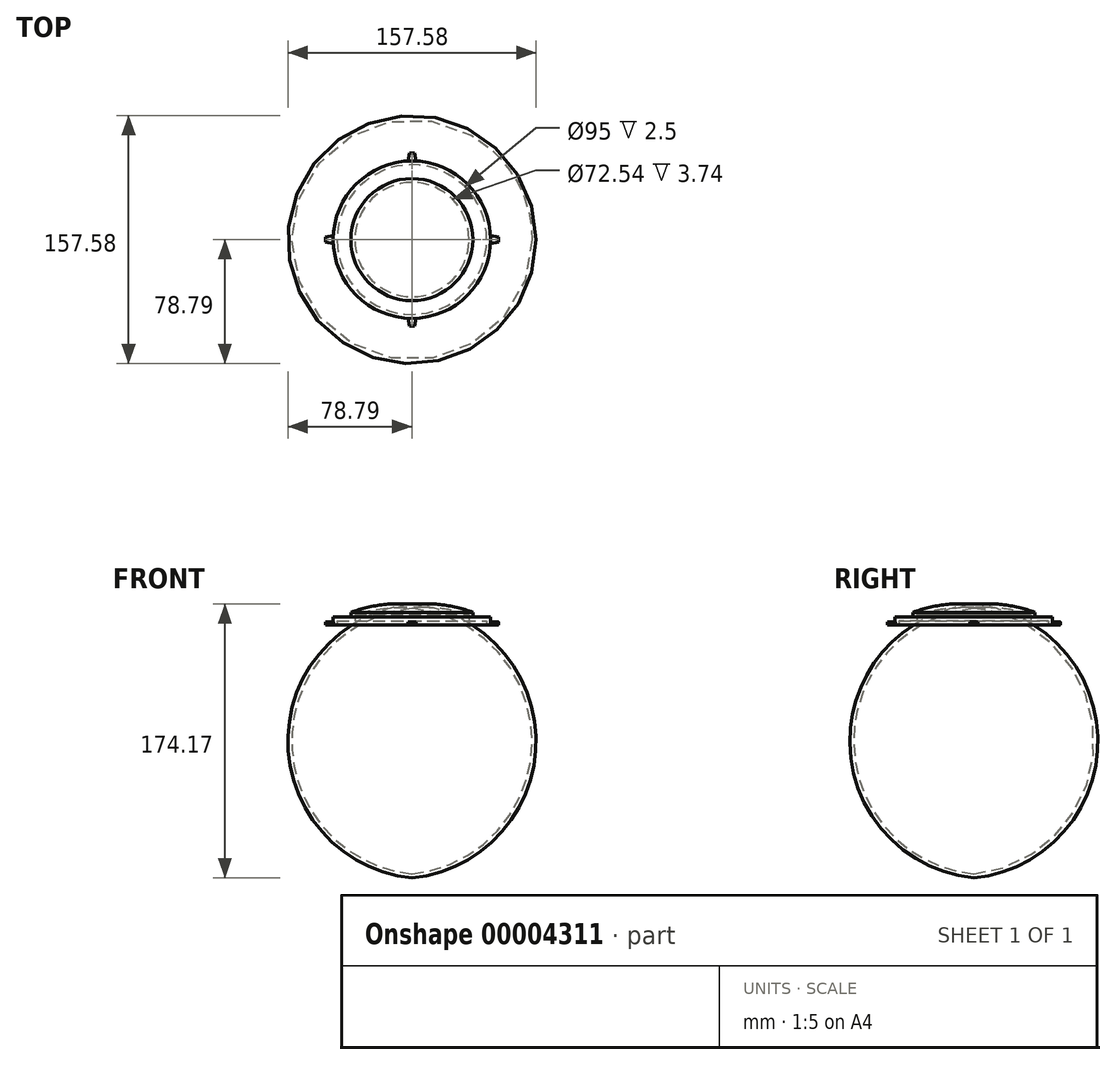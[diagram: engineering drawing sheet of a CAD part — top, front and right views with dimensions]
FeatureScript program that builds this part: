
annotation { "Feature Type Name" : "Feature", "Feature Type Description" : "" }
export const myFeature = defineFeature(function(context is Context, id is Id, definition is map)
    precondition{}
    {
        {
            var Q0;
            Q0=qCreatedBy(makeId("Front.planeOp"),FACE);
            var sketch = newSketch(context, id + "F0", { "sketchPlane" : qUnion([Q0])});
            skLineSegment(sketch, "E0", {"start": v(0, 0) * mm, "end": v(-50, 0) * mm});
            skLineSegment(sketch, "E1", {"start": v(-50, 0) * mm, "end": v(-55, 0) * mm});
            skArc(sketch, "E2", {"start": v(0, 13) * mm, "mid": v(-19.67, 12.7) * mm, "end": v(-38.77, 8) * mm});
            skLineSegment(sketch, "E3", {"start": v(0, 0) * mm, "end": v(0, 13) * mm});
            skLineSegment(sketch, "E4.0", {"start": v(-50, 2) * mm, "end": v(-55, 2) * mm});
            skLineSegment(sketch, "E5", {"start": v(-55, 2) * mm, "end": v(-55, 0) * mm});
            skLineSegment(sketch, "E6", {"start": v(-50, 2) * mm, "end": v(-50, 2.92) * mm});
            skLineSegment(sketch, "E7.0", {"start": v(0, 5) * mm, "end": v(-50, 5) * mm});
            skLineSegment(sketch, "E8.0", {"start": v(4.8, 8) * mm, "end": v(-50, 8) * mm});
            skLineSegment(sketch, "E9", {"start": v(-38.77, 8) * mm, "end": v(-38.77, 5) * mm});
            skArc(sketch, "E10.trimOffspring", {"start": v(-45.9, 5) * mm, "mid": v(-47.96, 3.99) * mm, "end": v(-50, 2.92) * mm, "construction": true});
            skLineSegment(sketch, "E11", {"start": v(0, 0) * mm, "end": v(55, 0) * mm});
            skLineSegment(sketch, "E12.0", {"start": v(0, 2) * mm, "end": v(55, 2) * mm});
            skLineSegment(sketch, "E13.0", {"start": v(0, 5) * mm, "end": v(55, 5) * mm});
            skLineSegment(sketch, "E14", {"start": v(-50, 5) * mm, "end": v(-50, 2.92) * mm});
            skSolve(sketch);
        }
        {
            var Q0;
            Q0=qCreatedBy(makeId("Top.planeOp"),FACE);
            var sketch = newSketch(context, id + "F1", { "sketchPlane" : qUnion([Q0])});
            skLineSegment(sketch, "E15.0", {"start": v(-50, 50) * mm, "end": v(-50, -50) * mm, "construction": true});
            skLineSegment(sketch, "E16.0", {"start": v(50, 50) * mm, "end": v(50, -50) * mm, "construction": true});
            skLineSegment(sketch, "E17.0", {"start": v(-50, -50) * mm, "end": v(50, -50) * mm, "construction": true});
            skLineSegment(sketch, "E18.0", {"start": v(-50, 50) * mm, "end": v(50, 50) * mm, "construction": true});
            skLineSegment(sketch, "E19.0", {"start": v(-5, 55) * mm, "end": v(-5, 49.75) * mm, "construction": true});
            skLineSegment(sketch, "E20.0", {"start": v(5, 55) * mm, "end": v(5, 49.75) * mm, "construction": true});
            skLineSegment(sketch, "E21.trimOffspring", {"start": v(-5, -49.75) * mm, "end": v(-5, -55) * mm, "construction": true});
            skLineSegment(sketch, "E22.trimOffspring", {"start": v(5, -49.75) * mm, "end": v(5, -55) * mm, "construction": true});
            skLineSegment(sketch, "E23.trimOffspring", {"start": v(49.75, 5) * mm, "end": v(55, 5) * mm, "construction": true});
            skLineSegment(sketch, "E24.0", {"start": v(-55, 55) * mm, "end": v(-55, -55) * mm, "construction": true});
            skLineSegment(sketch, "E25.0", {"start": v(-55, -55) * mm, "end": v(55, -55) * mm, "construction": true});
            skLineSegment(sketch, "E26.0", {"start": v(55, 55) * mm, "end": v(55, -55) * mm, "construction": true});
            skLineSegment(sketch, "E27.0", {"start": v(-55, 55) * mm, "end": v(55, 55) * mm, "construction": true});
            skLineSegment(sketch, "E28.0", {"start": v(-55, 0) * mm, "end": v(-50, 0) * mm, "construction": true});
            skCircle(sketch, "E29", {"center": v(0, 0) * mm, "radius": 55 * mm});
            skCircle(sketch, "E30", {"center": v(0, 0) * mm, "radius": 50 * mm});
            skLineSegment(sketch, "E31.0", {"start": v(0, -50) * mm, "end": v(0, -55) * mm, "construction": true});
            skLineSegment(sketch, "E32.0", {"start": v(50, 0) * mm, "end": v(55, 0) * mm, "construction": true});
            skLineSegment(sketch, "E33.0", {"start": v(0, 55) * mm, "end": v(0, 50) * mm, "construction": true});
            skLineSegment(sketch, "E34.0", {"start": v(50, -1.5) * mm, "end": v(55, -1.5) * mm, "construction": true});
            skLineSegment(sketch, "E35.0", {"start": v(50, 1.5) * mm, "end": v(55, 1.5) * mm, "construction": true});
            skLineSegment(sketch, "E36.0", {"start": v(49.04, 2.5) * mm, "end": v(55, 2.5) * mm, "construction": true});
            skLineSegment(sketch, "E37.0", {"start": v(49.48, -2.5) * mm, "end": v(55, -2.5) * mm, "construction": true});
            skLineSegment(sketch, "E38", {"start": v(-49.26, 2.64) * mm, "end": v(-55, 1.49) * mm});
            skLineSegment(sketch, "E39", {"start": v(-49.38, -2.6) * mm, "end": v(-55, -1.49) * mm});
            skLineSegment(sketch, "E40", {"start": v(48.47, -2.78) * mm, "end": v(55, -1.49) * mm});
            skLineSegment(sketch, "E41", {"start": v(48.17, 2.84) * mm, "end": v(55, 1.49) * mm});
            skLineSegment(sketch, "E42.0", {"start": v(-1.5, -48.6) * mm, "end": v(-1.5, -55) * mm, "construction": true});
            skLineSegment(sketch, "E43.0", {"start": v(1.5, -48.4) * mm, "end": v(1.5, -55) * mm, "construction": true});
            skLineSegment(sketch, "E44.0", {"start": v(-2.5, -48.6) * mm, "end": v(-2.5, -55) * mm, "construction": true});
            skLineSegment(sketch, "E45.0", {"start": v(2.5, -48.4) * mm, "end": v(2.5, -55) * mm, "construction": true});
            skLineSegment(sketch, "E46", {"start": v(-2.73, -48.72) * mm, "end": v(-1.49, -55) * mm});
            skLineSegment(sketch, "E47", {"start": v(2.75, -48.63) * mm, "end": v(1.49, -55) * mm});
            skLineSegment(sketch, "E48.0", {"start": v(-1.5, 55) * mm, "end": v(-1.5, 49.02) * mm, "construction": true});
            skLineSegment(sketch, "E49.0", {"start": v(1.5, 55) * mm, "end": v(1.5, 49.18) * mm, "construction": true});
            skLineSegment(sketch, "E50.0", {"start": v(-2.5, 55) * mm, "end": v(-2.5, 49.16) * mm, "construction": true});
            skLineSegment(sketch, "E51.0", {"start": v(2.5, 55) * mm, "end": v(2.5, 49.11) * mm, "construction": true});
            skLineSegment(sketch, "E52", {"start": v(-2.75, 48.62) * mm, "end": v(-1.49, 55) * mm});
            skLineSegment(sketch, "E53", {"start": v(2.77, 48.54) * mm, "end": v(1.49, 55) * mm});
            skCircle(sketch, "E54.0", {"center": v(0, 0) * mm, "radius": 54.9 * mm});
            skSolve(sketch);
        }
        {
            var Q0;
            {var subQ6=sQuery(id+"F0.wireOp",EDGE,"E0");Q0=makeQuery(id+"F0.imprint","IMPRINT",FACE,{"disambiguationData":[TD([[makeQuery(id+"F0.imprint","IMPRINT",EDGE,{"derivedFrom":subQ6}),-1.0]])]});}
            var Q1;
            {var subQ0=sQuery(id+"F0.wireOp",EDGE,"E9");Q1=makeQuery(id+"F0.imprint","IMPRINT",FACE,{"disambiguationData":[TD([[makeQuery(id+"F0.imprint","IMPRINT",EDGE,{"derivedFrom":subQ0}),1.0]])]});}
            var Q2;
            {var subQ3=sQuery(id+"F0.wireOp",EDGE,"E2");Q2=makeQuery(id+"F0.imprint","IMPRINT",FACE,{"disambiguationData":[TD([[makeQuery(id+"F0.imprint","IMPRINT",EDGE,{"derivedFrom":subQ3}),1.0]])]});}
            var Q3;
            Q3=sQuery(id+"F0.wireOp",EDGE,"E3");
            revolve(context, id + "F2", {"entities" : qUnion([Q0, Q1, Q2]), "axis" : qUnion([Q3]), "revolveType" : RevolveType.FULL});
        }
        {
            var Q0;
            {var subQ3=sQuery(id+"F1.wireOp",EDGE,"E39");var subQ5=sQuery(id+"F1.wireOp",EDGE,"E30");var subQ7=makeQuery(id+"F1.imprint","INTERSECT",VERTEX,{"derivedFrom":[subQ5,subQ3]});Q0=makeQuery(id+"F1.imprint","IMPRINT",FACE,{"disambiguationData":[TD([[makeQuery(id+"F1.imprint","IMPRINT",EDGE,{"disambiguationData":[TD([[subQ7,-1.0]])],"derivedFrom":subQ5}),-1.0]])]});}
            var Q1;
            {var subQ1=sQuery(id+"F1.wireOp",EDGE,"E52");var subQ5=sQuery(id+"F1.wireOp",EDGE,"E30");var subQ6=makeQuery(id+"F1.imprint","INTERSECT",VERTEX,{"derivedFrom":[subQ5,subQ1]});Q1=makeQuery(id+"F1.imprint","IMPRINT",FACE,{"disambiguationData":[TD([[makeQuery(id+"F1.imprint","IMPRINT",EDGE,{"disambiguationData":[TD([[subQ6,-1.0]])],"derivedFrom":subQ5}),-1.0]])]});}
            var Q2;
            {var subQ1=sQuery(id+"F1.wireOp",EDGE,"E53");var subQ5=sQuery(id+"F1.wireOp",EDGE,"E30");var subQ6=makeQuery(id+"F1.imprint","INTERSECT",VERTEX,{"derivedFrom":[subQ5,subQ1]});Q2=makeQuery(id+"F1.imprint","IMPRINT",FACE,{"disambiguationData":[TD([[makeQuery(id+"F1.imprint","IMPRINT",EDGE,{"disambiguationData":[TD([[subQ6,1.0]])],"derivedFrom":subQ5}),-1.0]])]});}
            var Q3;
            {var subQ1=sQuery(id+"F1.wireOp",EDGE,"E47");var subQ5=sQuery(id+"F1.wireOp",EDGE,"E30");var subQ6=makeQuery(id+"F1.imprint","INTERSECT",VERTEX,{"derivedFrom":[subQ5,subQ1]});Q3=makeQuery(id+"F1.imprint","IMPRINT",FACE,{"disambiguationData":[TD([[makeQuery(id+"F1.imprint","IMPRINT",EDGE,{"disambiguationData":[TD([[subQ6,-1.0]])],"derivedFrom":subQ5}),-1.0]])]});}
            var Q4;
            {var subQ3=sQuery(id+"F1.wireOp",EDGE,"E39");var subQ5=sQuery(id+"F1.wireOp",EDGE,"E29");var subQ7=makeQuery(id+"F1.imprint","INTERSECT",VERTEX,{"derivedFrom":[subQ3,subQ5]});Q4=makeQuery(id+"F1.imprint","IMPRINT",FACE,{"disambiguationData":[TD([[makeQuery(id+"F1.imprint","IMPRINT",EDGE,{"disambiguationData":[TD([[subQ7,1.0]])],"derivedFrom":subQ3}),1.0]])]});}
            var Q5;
            {var subQ0=sQuery(id+"F1.wireOp",EDGE,"E29");var subQ3=sQuery(id+"F1.wireOp",EDGE,"E38");var subQ4=makeQuery(id+"F1.imprint","INTERSECT",VERTEX,{"derivedFrom":[subQ3,subQ0]});Q5=makeQuery(id+"F1.imprint","IMPRINT",FACE,{"disambiguationData":[TD([[makeQuery(id+"F1.imprint","IMPRINT",EDGE,{"disambiguationData":[TD([[subQ4,1.0]])],"derivedFrom":subQ3}),1.0]])]});}
            var Q6;
            {var subQ3=sQuery(id+"F1.wireOp",EDGE,"E38");var subQ5=sQuery(id+"F1.wireOp",EDGE,"E29");var subQ7=makeQuery(id+"F1.imprint","INTERSECT",VERTEX,{"derivedFrom":[subQ3,subQ5]});Q6=makeQuery(id+"F1.imprint","IMPRINT",FACE,{"disambiguationData":[TD([[makeQuery(id+"F1.imprint","IMPRINT",EDGE,{"disambiguationData":[TD([[subQ7,1.0]])],"derivedFrom":subQ3}),-1.0]])]});}
            var Q7;
            {var subQ3=sQuery(id+"F1.wireOp",EDGE,"E52");var subQ5=sQuery(id+"F1.wireOp",EDGE,"E29");var subQ7=makeQuery(id+"F1.imprint","INTERSECT",VERTEX,{"derivedFrom":[subQ3,subQ5]});Q7=makeQuery(id+"F1.imprint","IMPRINT",FACE,{"disambiguationData":[TD([[makeQuery(id+"F1.imprint","IMPRINT",EDGE,{"disambiguationData":[TD([[subQ7,1.0]])],"derivedFrom":subQ3}),-1.0]])]});}
            var Q8;
            {var subQ3=sQuery(id+"F1.wireOp",EDGE,"E41");var subQ5=sQuery(id+"F1.wireOp",EDGE,"E29");var subQ7=makeQuery(id+"F1.imprint","INTERSECT",VERTEX,{"derivedFrom":[subQ3,subQ5]});Q8=makeQuery(id+"F1.imprint","IMPRINT",FACE,{"disambiguationData":[TD([[makeQuery(id+"F1.imprint","IMPRINT",EDGE,{"disambiguationData":[TD([[subQ7,1.0]])],"derivedFrom":subQ3}),1.0]])]});}
            var Q9;
            {var subQ0=sQuery(id+"F1.wireOp",EDGE,"E29");var subQ3=sQuery(id+"F1.wireOp",EDGE,"E40");var subQ4=makeQuery(id+"F1.imprint","INTERSECT",VERTEX,{"derivedFrom":[subQ3,subQ0]});Q9=makeQuery(id+"F1.imprint","IMPRINT",FACE,{"disambiguationData":[TD([[makeQuery(id+"F1.imprint","IMPRINT",EDGE,{"disambiguationData":[TD([[subQ4,1.0]])],"derivedFrom":subQ3}),-1.0]])]});}
            var Q10;
            {var subQ3=sQuery(id+"F1.wireOp",EDGE,"E40");var subQ5=sQuery(id+"F1.wireOp",EDGE,"E29");var subQ7=makeQuery(id+"F1.imprint","INTERSECT",VERTEX,{"derivedFrom":[subQ3,subQ5]});Q10=makeQuery(id+"F1.imprint","IMPRINT",FACE,{"disambiguationData":[TD([[makeQuery(id+"F1.imprint","IMPRINT",EDGE,{"disambiguationData":[TD([[subQ7,1.0]])],"derivedFrom":subQ3}),1.0]])]});}
            var Q11;
            {var subQ3=sQuery(id+"F1.wireOp",EDGE,"E46");var subQ5=sQuery(id+"F1.wireOp",EDGE,"E29");var subQ7=makeQuery(id+"F1.imprint","INTERSECT",VERTEX,{"derivedFrom":[subQ3,subQ5]});Q11=makeQuery(id+"F1.imprint","IMPRINT",FACE,{"disambiguationData":[TD([[makeQuery(id+"F1.imprint","IMPRINT",EDGE,{"disambiguationData":[TD([[subQ7,1.0]])],"derivedFrom":subQ3}),1.0]])]});}
            extrude(context, id + "F3", {"entities" : qUnion([Q0, Q1, Q2, Q3, Q4, Q5, Q6, Q7, Q8, Q9, Q10, Q11]), "operationType" : NewBodyOperationType.REMOVE, "depth" : 25 * mm});
        }
        {
            var Q0;
            Q0=makeQuery(id+"F2.opRevolve","SWEPT_FACE",FACE,{"disambiguationData":[OSD([sQuery(id+"F0.wireOp",EDGE,"E0"),sQuery(id+"F0.wireOp",EDGE,"E1")])]});
            shell(context, id + "F4", {"entities" : qUnion([Q0]), "thickness" : 2.5 * mm});
        }
    });
